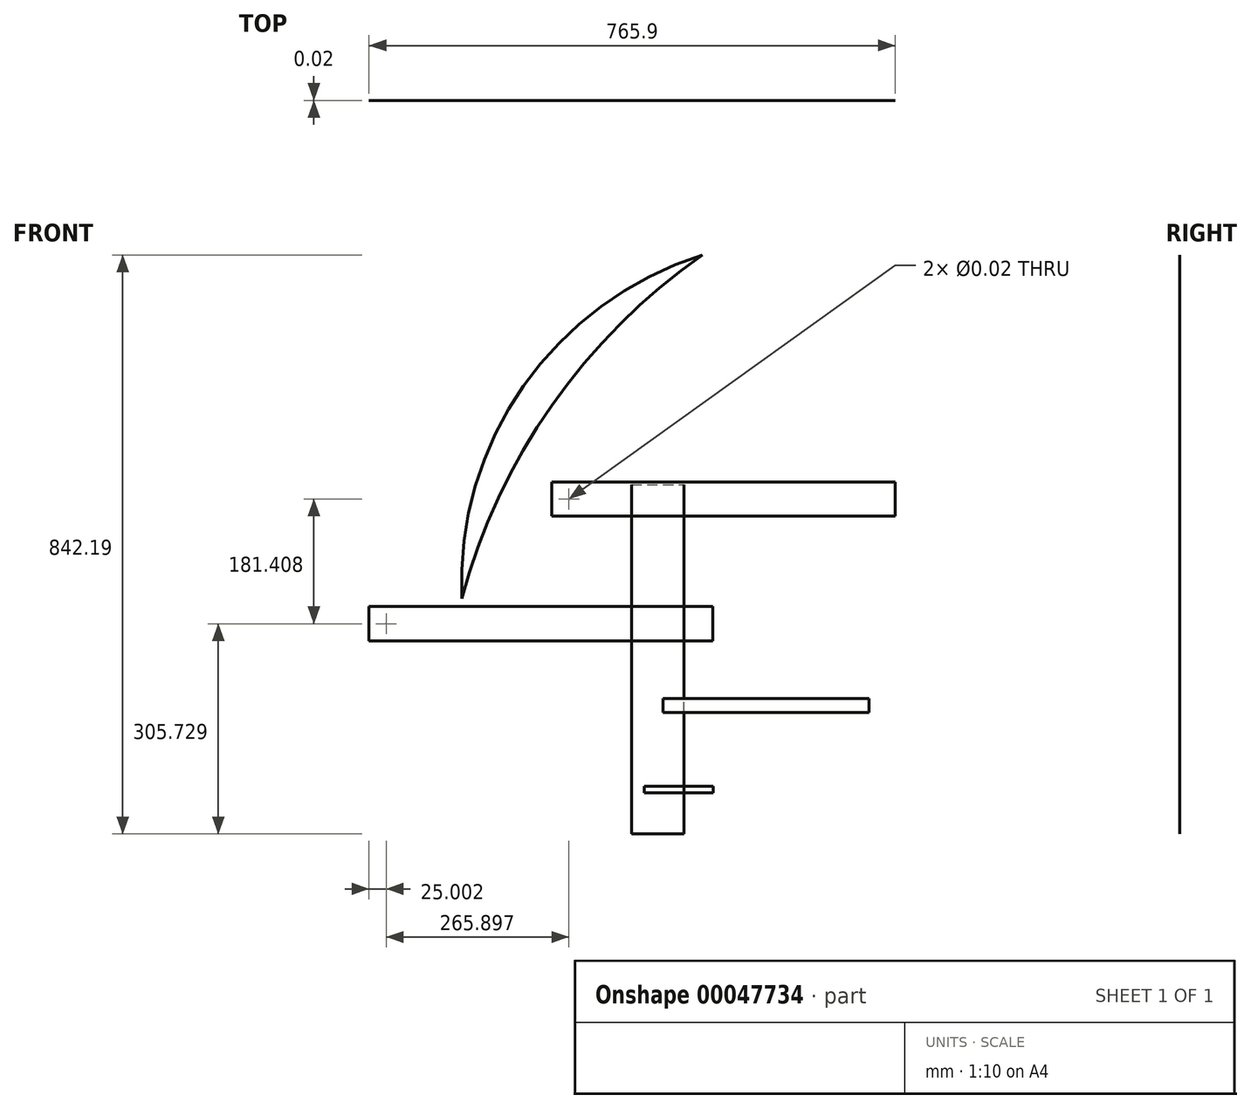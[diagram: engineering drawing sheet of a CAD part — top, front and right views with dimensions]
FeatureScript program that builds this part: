
annotation { "Feature Type Name" : "Feature", "Feature Type Description" : "" }
export const myFeature = defineFeature(function(context is Context, id is Id, definition is map)
    precondition{}
    {
        {
            assignVariable(context, id + "F0", {"name" : "ThicknessHardboard", "anyValue" : 3 / 406.4 * mm});
        }
        {
            assignVariable(context, id + "F1", {"name" : "DiameterHole", "anyValue" : 0.02});
        }
        {
            var Q0;
            Q0=qCreatedBy(makeId("Front.planeOp"),FACE);
            var sketch = newSketch(context, id + "F2", { "sketchPlane" : qUnion([Q0])});
            skLineSegment(sketch, "E0.bottom", {"start": v(0, 0) * mm, "end": v(76.2, 0) * mm});
            skLineSegment(sketch, "E0.top", {"start": v(0, 508) * mm, "end": v(76.2, 508) * mm});
            skLineSegment(sketch, "E0.left", {"start": v(0, 0) * mm, "end": v(0, 508) * mm});
            skLineSegment(sketch, "E0.right", {"start": v(76.2, 0) * mm, "end": v(76.2, 508) * mm});
            skSolve(sketch);
        }
        {
            var Q0;
            Q0=makeQuery(id+"F2.imprint","IMPRINT",FACE,{"disambiguationData":[TD([[makeQuery(id+"F2.imprint","IMPRINT",EDGE,{"derivedFrom":sQuery(id+"F2.wireOp",EDGE,"E0.bottom")}),1.0]])]});
            extrude(context, id + "F3", {"entities" : qUnion([Q0]), "oppositeDirection" : true, "depth" : getVariable(context, 'ThicknessHardboard')});
        }
        {
            var Q0;
            Q0=qCreatedBy(makeId("Front.planeOp"),FACE);
            var sketch = newSketch(context, id + "F4", { "sketchPlane" : qUnion([Q0])});
            skLineSegment(sketch, "E1.bottom", {"start": v(18.8, 69.52) * mm, "end": v(118.8, 69.52) * mm});
            skLineSegment(sketch, "E1.top", {"start": v(18.8, 59.52) * mm, "end": v(118.8, 59.52) * mm});
            skLineSegment(sketch, "E1.left", {"start": v(18.8, 69.52) * mm, "end": v(18.8, 59.52) * mm});
            skLineSegment(sketch, "E1.right", {"start": v(118.8, 69.52) * mm, "end": v(118.8, 59.52) * mm});
            skSolve(sketch);
        }
        {
            var Q0;
            Q0=makeQuery(id+"F4.imprint","IMPRINT",FACE,{"disambiguationData":[TD([[makeQuery(id+"F4.imprint","IMPRINT",EDGE,{"derivedFrom":sQuery(id+"F4.wireOp",EDGE,"E1.bottom")}),-1.0]])]});
            extrude(context, id + "F5", {"entities" : qUnion([Q0]), "depth" : getVariable(context, 'ThicknessHardboard')});
        }
        {
            var Q0;
            Q0=qCreatedBy(makeId("Front.planeOp"),FACE);
            var sketch = newSketch(context, id + "F6", { "sketchPlane" : qUnion([Q0])});
            skLineSegment(sketch, "E2.bottom", {"start": v(45.82, 196.72) * mm, "end": v(345.82, 196.72) * mm});
            skLineSegment(sketch, "E2.top", {"start": v(45.82, 176.72) * mm, "end": v(345.82, 176.72) * mm});
            skLineSegment(sketch, "E2.left", {"start": v(45.82, 196.72) * mm, "end": v(45.82, 176.72) * mm});
            skLineSegment(sketch, "E2.right", {"start": v(345.82, 196.72) * mm, "end": v(345.82, 176.72) * mm});
            skSolve(sketch);
        }
        {
            var Q0;
            Q0=qSketchRegion(id+"F6",true);
            extrude(context, id + "F7", {"entities" : qUnion([Q0]), "operationType" : NewBodyOperationType.ADD, "depth" : getVariable(context, 'ThicknessHardboard')});
        }
        {
            var Q0;
            Q0=qCreatedBy(makeId("Front.planeOp"),FACE);
            var sketch = newSketch(context, id + "F8", { "sketchPlane" : qUnion([Q0])});
            skArc(sketch, "E3", {"start": v(103.43, 842.19) * mm, "mid": v(-156.88, 651.86) * mm, "end": v(-246.86, 342.19) * mm});
            skArc(sketch, "E4", {"start": v(103.43, 842.19) * mm, "mid": v(-115.93, 623.17) * mm, "end": v(-246.86, 342.19) * mm});
            skSolve(sketch);
        }
        {
            var Q0;
            Q0=qSketchRegion(id+"F8",true);
            extrude(context, id + "F9", {"entities" : qUnion([Q0]), "depth" : getVariable(context, 'ThicknessHardboard')});
        }
        {
            var Q0;
            Q0=qCreatedBy(makeId("Front.planeOp"),FACE);
            var sketch = newSketch(context, id + "F10", { "sketchPlane" : qUnion([Q0])});
            skLineSegment(sketch, "E5.bottom", {"start": v(-116, 512.14) * mm, "end": v(384, 512.14) * mm});
            skLineSegment(sketch, "E5.top", {"start": v(-116, 462.14) * mm, "end": v(384, 462.14) * mm});
            skLineSegment(sketch, "E5.left", {"start": v(-116, 512.14) * mm, "end": v(-116, 462.14) * mm});
            skLineSegment(sketch, "E5.right", {"start": v(384, 512.14) * mm, "end": v(384, 462.14) * mm});
            skPoint(sketch, "E6", {"position": v(0, 0) * mm});
            skSolve(sketch);
        }
        {
            var Q0;
            Q0=makeQuery(id+"F10.imprint","IMPRINT",FACE,{"disambiguationData":[TD([[makeQuery(id+"F10.imprint","IMPRINT",EDGE,{"derivedFrom":sQuery(id+"F10.wireOp",EDGE,"E5.bottom")}),-1.0]])]});
            extrude(context, id + "F11", {"entities" : qUnion([Q0]), "depth" : getVariable(context, 'ThicknessHardboard')});
        }
        {
            var Q0;
            Q0=makeQuery(id+"F11.opExtrude","CAP_FACE",FACE,{"disambiguationData":[OSD([sQuery(id+"F10.wireOp",EDGE,"E5.bottom"),sQuery(id+"F10.wireOp",EDGE,"E5.top"),sQuery(id+"F10.wireOp",EDGE,"E5.left"),sQuery(id+"F10.wireOp",EDGE,"E5.right")])],"isStart":false});
            var sketch = newSketch(context, id + "F12", { "sketchPlane" : qUnion([Q0])});
            skPoint(sketch, "E7", {"position": v(-91, 487.14) * mm});
            skSolve(sketch);
        }
        {
            var Q0;
            Q0=sQuery(id+"F12.wireOp",VERTEX,"E7");
            var Q1;
            Q1=makeQuery(id+"F11.opExtrude","SWEPT_BODY",BODY,{"disambiguationData":[OSD([sQuery(id+"F10.wireOp",EDGE,"E5.bottom"),sQuery(id+"F10.wireOp",EDGE,"E5.top"),sQuery(id+"F10.wireOp",EDGE,"E5.left"),sQuery(id+"F10.wireOp",EDGE,"E5.right")])]});
            hole(context, id + "F13", {"style" : HoleStyle.SIMPLE, "holeDiameter" : (getVariable(context, 'DiameterHole')) * mm, "endStyle" : HoleEndStyle.THROUGH, "locations" : qUnion([Q0]), "scope" : qUnion([Q1])});
        }
        {
            var Q0;
            Q0=qCreatedBy(makeId("Front.planeOp"),FACE);
            var sketch = newSketch(context, id + "F14", { "sketchPlane" : qUnion([Q0])});
            skLineSegment(sketch, "E8.bottom", {"start": v(-381.9, 330.73) * mm, "end": v(118.1, 330.73) * mm});
            skLineSegment(sketch, "E8.top", {"start": v(-381.9, 280.73) * mm, "end": v(118.1, 280.73) * mm});
            skLineSegment(sketch, "E8.left", {"start": v(-381.9, 330.73) * mm, "end": v(-381.9, 280.73) * mm});
            skLineSegment(sketch, "E8.right", {"start": v(118.1, 330.73) * mm, "end": v(118.1, 280.73) * mm});
            skSolve(sketch);
        }
        {
            var Q0;
            Q0=qSketchRegion(id+"F14",true);
            extrude(context, id + "F15", {"entities" : qUnion([Q0]), "depth" : getVariable(context, 'ThicknessHardboard')});
        }
        {
            var Q0;
            Q0=makeQuery(id+"F15.opExtrude","CAP_FACE",FACE,{"disambiguationData":[OSD([sQuery(id+"F14.wireOp",EDGE,"E8.bottom"),sQuery(id+"F14.wireOp",EDGE,"E8.top"),sQuery(id+"F14.wireOp",EDGE,"E8.left"),sQuery(id+"F14.wireOp",EDGE,"E8.right")])],"isStart":false});
            var sketch = newSketch(context, id + "F16", { "sketchPlane" : qUnion([Q0])});
            skPoint(sketch, "E9", {"position": v(-356.9, 305.73) * mm});
            skSolve(sketch);
        }
        {
            var Q0;
            Q0=sQuery(id+"F16.wireOp",VERTEX,"E9");
            var Q1;
            Q1=makeQuery(id+"F15.opExtrude","SWEPT_BODY",BODY,{"disambiguationData":[OSD([sQuery(id+"F14.wireOp",EDGE,"E8.bottom"),sQuery(id+"F14.wireOp",EDGE,"E8.top"),sQuery(id+"F14.wireOp",EDGE,"E8.left"),sQuery(id+"F14.wireOp",EDGE,"E8.right")])]});
            hole(context, id + "F17", {"style" : HoleStyle.SIMPLE, "holeDiameter" : (getVariable(context, 'DiameterHole')) * mm, "endStyle" : HoleEndStyle.THROUGH, "locations" : qUnion([Q0]), "scope" : qUnion([Q1])});
        }
    });
